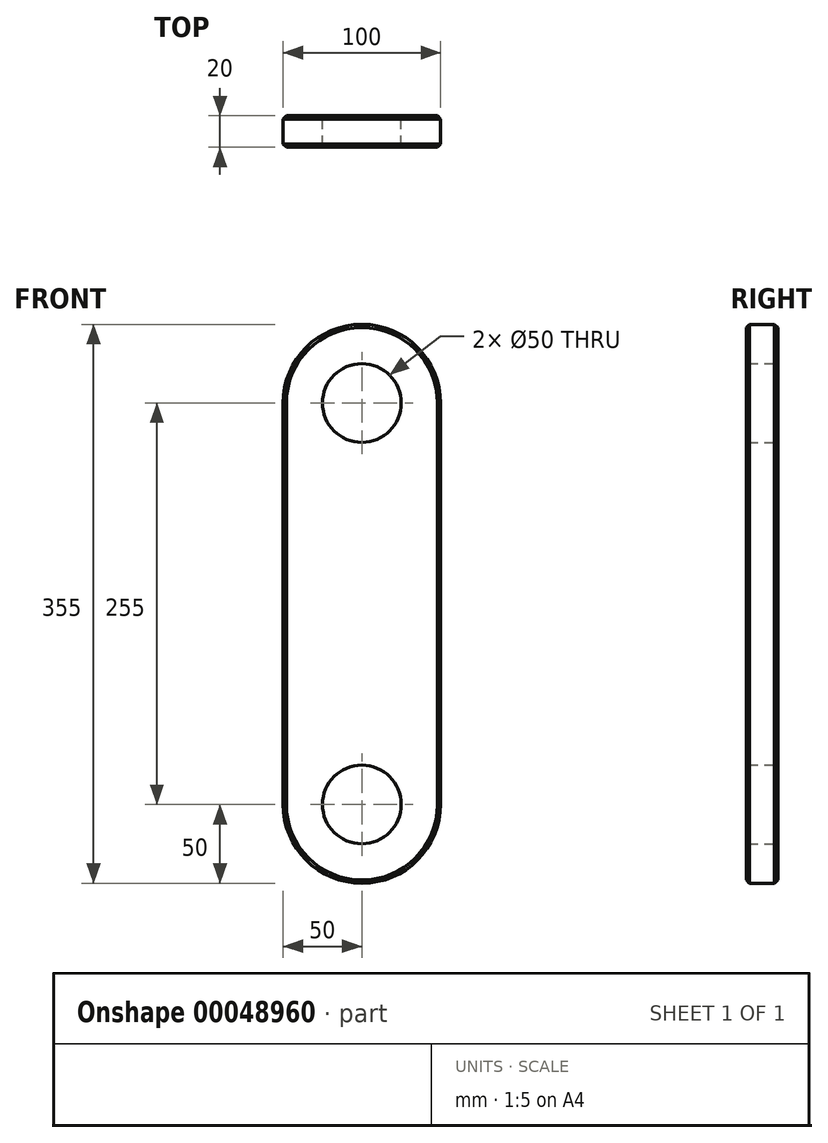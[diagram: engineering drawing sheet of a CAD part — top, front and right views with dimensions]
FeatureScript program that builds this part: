
annotation { "Feature Type Name" : "Feature", "Feature Type Description" : "" }
export const myFeature = defineFeature(function(context is Context, id is Id, definition is map)
    precondition{}
    {
        {
            var Q0;
            Q0=qCreatedBy(makeId("Front.planeOp"),FACE);
            var sketch = newSketch(context, id + "F0", { "sketchPlane" : qUnion([Q0])});
            skLineSegment(sketch, "E0.bottom", {"start": v(-50, 0) * mm, "end": v(50, 0) * mm, "construction": true});
            skLineSegment(sketch, "E0.top", {"start": v(-50, -255) * mm, "end": v(50, -255) * mm, "construction": true});
            skLineSegment(sketch, "E0.left", {"start": v(-50, 0) * mm, "end": v(-50, -255) * mm});
            skLineSegment(sketch, "E0.right", {"start": v(50, 0) * mm, "end": v(50, -255) * mm});
            skLineSegment(sketch, "E1", {"start": v(0, 0) * mm, "end": v(0, -255) * mm, "construction": true});
            skArc(sketch, "E2", {"start": v(50, 0) * mm, "mid": v(0, 50) * mm, "end": v(-50, 0) * mm});
            skArc(sketch, "E3", {"start": v(-50, -255) * mm, "mid": v(0, -305) * mm, "end": v(50, -255) * mm});
            skCircle(sketch, "E4", {"center": v(0, 0) * mm, "radius": 25 * mm});
            skCircle(sketch, "E5", {"center": v(0, -255) * mm, "radius": 25 * mm});
            skSolve(sketch);
        }
        {
            var Q0;
            Q0=makeQuery(id+"F0.imprint","IMPRINT",FACE,{"disambiguationData":[TD([[makeQuery(id+"F0.imprint","IMPRINT",EDGE,{"derivedFrom":sQuery(id+"F0.wireOp",EDGE,"E0.left")}),1.0]])]});
            extrude(context, id + "F1", {"entities" : qUnion([Q0]), "depth" : 20 * mm});
        }
        {
            var Q0;
            Q0=makeQuery(id+"F1.opExtrude","CAP_EDGE",EDGE,{"disambiguationData":[OSD([sQuery(id+"F0.wireOp",EDGE,"E0.left")])],"isStart":false});
            var Q1;
            Q1=makeQuery(id+"F1.opExtrude","CAP_EDGE",EDGE,{"disambiguationData":[OSD([sQuery(id+"F0.wireOp",EDGE,"E2")])],"isStart":false});
            var Q2;
            Q2=makeQuery(id+"F1.opExtrude","CAP_EDGE",EDGE,{"disambiguationData":[OSD([sQuery(id+"F0.wireOp",EDGE,"E0.right")])],"isStart":false});
            var Q3;
            Q3=makeQuery(id+"F1.opExtrude","CAP_EDGE",EDGE,{"disambiguationData":[OSD([sQuery(id+"F0.wireOp",EDGE,"E3")])],"isStart":false});
            var Q4;
            Q4=makeQuery(id+"F1.opExtrude","CAP_EDGE",EDGE,{"disambiguationData":[OSD([sQuery(id+"F0.wireOp",EDGE,"E3")])],"isStart":true});
            var Q5;
            Q5=makeQuery(id+"F1.opExtrude","CAP_EDGE",EDGE,{"disambiguationData":[OSD([sQuery(id+"F0.wireOp",EDGE,"E0.left")])],"isStart":true});
            var Q6;
            Q6=makeQuery(id+"F1.opExtrude","CAP_EDGE",EDGE,{"disambiguationData":[OSD([sQuery(id+"F0.wireOp",EDGE,"E2")])],"isStart":true});
            var Q7;
            Q7=makeQuery(id+"F1.opExtrude","CAP_EDGE",EDGE,{"disambiguationData":[OSD([sQuery(id+"F0.wireOp",EDGE,"E0.right")])],"isStart":true});
            chamfer(context, id + "F2", {"entities" : qUnion([Q0, Q1, Q2, Q3, Q4, Q5, Q6, Q7]), "chamferType" : ChamferType.OFFSET_ANGLE, "width" : 2 * mm, "oppositeDirection" : false, "angle" : 45 * degree, "tangentPropagation" : true});
        }
    });
